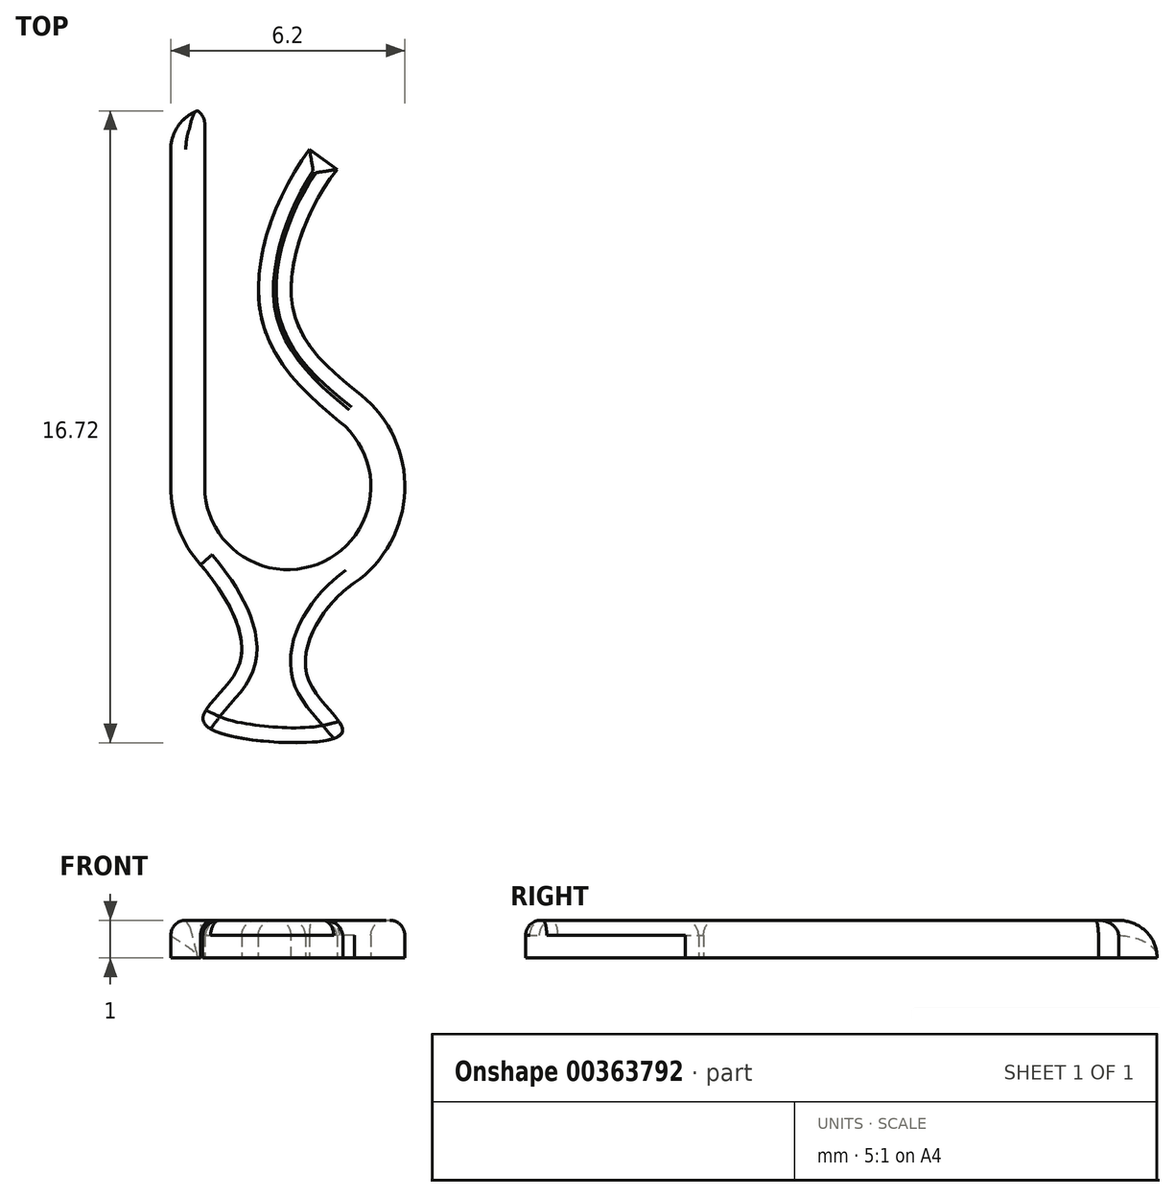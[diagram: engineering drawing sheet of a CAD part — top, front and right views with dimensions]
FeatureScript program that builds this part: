
annotation { "Feature Type Name" : "Feature", "Feature Type Description" : "" }
export const myFeature = defineFeature(function(context is Context, id is Id, definition is map)
    precondition{}
    {
        {
            var Q0;
            Q0=qCreatedBy(makeId("Top.planeOp"),FACE);
            var sketch = newSketch(context, id + "F0", { "sketchPlane" : qUnion([Q0])});
            skLineSegment(sketch, "E0", {"start": v(0, 0) * mm, "end": v(0, 10) * mm});
            skFitSpline(sketch, "E1", {"points": [v(3.58, 1.72) * mm, v(1.46, 4.66) * mm, v(2.78, 8.92) * mm], "startDerivative": vector(-7.2, 5.78) * mm, "endDerivative": vector(5.57, 7.57) * mm});
            skArc(sketch, "E2", {"start": v(0, 0) * mm, "mid": v(3.15, -1.98) * mm, "end": v(3.58, 1.72) * mm});
            skArc(sketch, "E3", {"start": v(3.58, 1.72) * mm, "mid": v(1.25, 1.98) * mm, "end": v(0, 0) * mm, "construction": true});
            skFitSpline(sketch, "E4.0", {"points": [v(4.14, 2.42) * mm, v(3.86, 2.65) * mm, v(3.35, 3.09) * mm, v(2.8, 3.7) * mm, v(2.46, 4.3) * mm, v(2.3, 4.91) * mm, v(2.32, 5.7) * mm, v(2.54, 6.6) * mm, v(2.93, 7.52) * mm, v(3.3, 8.11) * mm, v(3.5, 8.4) * mm]});
            skArc(sketch, "E4.1", {"start": v(-0.9, 0) * mm, "mid": v(-0.7, -1.1) * mm, "end": v(-0.1, -2.07) * mm});
            skLineSegment(sketch, "E4.2", {"start": v(-0.9, 0) * mm, "end": v(-0.9, 10) * mm});
            skLineSegment(sketch, "E5", {"start": v(0, 10) * mm, "end": v(-0.9, 10) * mm});
            skLineSegment(sketch, "E6", {"start": v(2.78, 8.92) * mm, "end": v(3.5, 8.4) * mm});
            skFitSpline(sketch, "E7", {"points": [v(3.97, -2.55) * mm, v(2.74, -5.08) * mm, v(3.6, -6.56) * mm, v(0, -6.3) * mm, v(0.9, -4.75) * mm, v(-0.1, -2.07) * mm], "startDerivative": vector(-11.07, -7.48) * mm, "endDerivative": vector(-8.47, 10) * mm});
            skArc(sketch, "E8", {"start": v(3.97, -2.55) * mm, "mid": v(5.3, -0.1) * mm, "end": v(4.14, 2.42) * mm});
            skArc(sketch, "E9", {"start": v(-0.1, -2.07) * mm, "mid": v(1.84, -3.08) * mm, "end": v(3.97, -2.55) * mm, "construction": true});
            skSolve(sketch);
        }
        {
            var Q0;
            Q0=makeQuery(id+"F0.imprint","IMPRINT",FACE,{"disambiguationData":[TD([[makeQuery(id+"F0.imprint","IMPRINT",EDGE,{"derivedFrom":sQuery(id+"F0.wireOp",EDGE,"E0")}),1.0]])]});
            extrude(context, id + "F1", {"entities" : qUnion([Q0]), "depth" : 1 * mm});
        }
        {
            var Q0;
            Q0=makeQuery(id+"F1.opExtrude","SWEPT_EDGE",EDGE,{"disambiguationData":[OSD([sQuery(id+"F0.wireOp",EDGE,"E4.2"),sQuery(id+"F0.wireOp",EDGE,"E5")])]});
            var Q1;
            Q1=makeQuery(id+"F1.opExtrude","CAP_EDGE",EDGE,{"disambiguationData":[OSD([sQuery(id+"F0.wireOp",EDGE,"E5")])],"isStart":false});
            fillet(context, id + "F2", {"entities" : qUnion([Q0, Q1]), "radius" : 1.1 * mm, "tangentPropagation" : true, "allowEdgeOverflow" : false});
        }
        {
            var Q0;
            Q0=makeQuery(id+"F1.opExtrude","CAP_FACE",FACE,{"disambiguationData":[OSD([sQuery(id+"F0.wireOp",EDGE,"E0"),sQuery(id+"F0.wireOp",EDGE,"E1"),sQuery(id+"F0.wireOp",EDGE,"E2"),sQuery(id+"F0.wireOp",EDGE,"E4.0"),sQuery(id+"F0.wireOp",EDGE,"E4.1"),sQuery(id+"F0.wireOp",EDGE,"E4.2"),sQuery(id+"F0.wireOp",EDGE,"E5"),sQuery(id+"F0.wireOp",EDGE,"E6"),sQuery(id+"F0.wireOp",EDGE,"E7"),sQuery(id+"F0.wireOp",EDGE,"E8")])],"isStart":false});
            fillet(context, id + "F3", {"entities" : qUnion([Q0]), "radius" : .4 * mm, "tangentPropagation" : true, "allowEdgeOverflow" : false});
        }
    });
